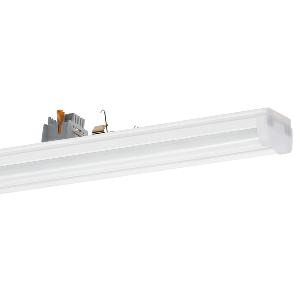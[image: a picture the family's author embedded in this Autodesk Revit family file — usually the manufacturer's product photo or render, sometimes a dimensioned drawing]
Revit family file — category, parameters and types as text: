
# Revit family: conveo_-_cvg_6000_827-865_d-c_da_7_226848499-00805631_feb6
name_source: partatom
category: Lighting Fixtures
units: mm (PartAtom-declared; Revit-internal decimal feet)

## family parameters
Cut with Voids When Loaded = No
Host = Face
Light Source = No
Part Type = Normal
Room Calculation Point = No
Round Connector Dimension = Use Diameter
Shared = No

## types (1)
- CONVEO - CVG 6000/827-865/D-C/DA/7 (1 x LED, 6500 lm, 2700-6500K)
    Apparent Load = 51 VA
    Approval mark = CE
    CIE Flux Codes = 48 76 92 91 100
    Color Rendering = 80-89
    Color Temperature = 2700-6500K
    Control Gear = Electronic ballast
    Default Elevation = 1800 mm
    Description = CVG 6000/827-865/D-C/DA/7|Continuous-row system|light source: LED|work equipment: Adjustable electronic ballast, digital DALI|connected load: 220-240 V, 50-60 Hz|Power consumption: approx. 51 W|luminous flux: 6500 lm|luminous efficacy: 127 lm/W|colour temperature: , ca. 2700-6500 K|color rendering index (CRI): >= 80|chromaticity tolerance:  3 SDCM|System of protection: IP 40|class of protection: I|technology: Continuously dimmable|luminaire body|material: Aluminium|surface: Powder coatet|colour: White|lamp cover: Acrylic (PMMA), Satine|weight (net): approx. 1.9 kg|Fastening: Available separately|minimum ambient temperature: -25 ░C|maximum ambient temperature: 43 ░C|special features: Specified values at approx. 4000 K, External control required for Dali Device type 8, Constant luminous flux between 2700 and 6500 K, Constant colour temperature over the whole dimming range|Approval mark: VDE - ENEC|
    Frequency = 50 Hz
    Height = 88 mm
    Lamp = 1 x LED
    Lamp Light Flux = 6500 lm
    Lamp count = 1
    Length = 1500 mm
    Luminous efficacy = 127 lm/W
    Manufacturer = Waldmann
    ModVariant = No
    Model = 226848499-00805631
    Mounting Place = Ceiling
    Mounting Type = Pendant
    Number of Poles = 1
    OnlyDefault = Yes
    Power Factor = 1
    Product Name = CONVEO - CVG 6000/827-865/D-C/DA/7
    Product group = Continuous-row system (industry)
    ProductGroupID = 301
    Protection Class = Protection class I
    Protection Degree = IP 40
    RLX_Detail_Level = 1
    RlxData = <blob elided: 64629 chars, md5=85022583>
    Socket = socket
    Standby Power = 0 W
    System Light Flux = 6500 lm
    System Power = 51 W
    Type Comments = Product without accessories
    Type Image = 226848499-00805631.jpg
    URL = http://relux.com
    VarID = ---
    Voltage = 230 V
    Voltage Range = 220-240 V
    Weight = 0.00 kg
    Width = 64 mm

## geometry (parser evidence)
native form markers: Blend x4, Sweep x12
no freeform markers — native parametric forms only
